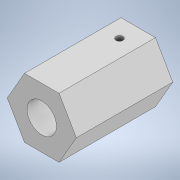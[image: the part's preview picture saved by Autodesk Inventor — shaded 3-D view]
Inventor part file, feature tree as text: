
AUTODESK INVENTOR PART (.ipt)
format: ipt  version: 2022 (Build 260153000, 153)  size: 137,728 bytes
history: native  units: mm
features: extrude x3, sketch x2
ambient origin geometry x8: Origin, YZ Plane, XZ Plane, XY Plane, X Axis, Y Axis, Z Axis, Center Point
bodies: Solid1 (feature_tree)
feature tree (5):
  sketch  "Sketch1"  dims[d0=5.5mm d2=3.1mm]
  extrude  "Extrusion1"  Depth=3.1mm
  extrude  "Extrusion2"  Depth=10.0mm
  extrude  "Extrusion3"  Depth=2.5mm
  sketch  "Sketch2"  dims[d3=60.0mm d5=360.0deg d7=0.4mm d8=2.5mm d9=8.0mm d10=0.0mm d11=10.0mm d12=0.0mm d13=1.3mm d14=6.5mm d15=15.0mm d16=0.0mm d4=0.5mm]
